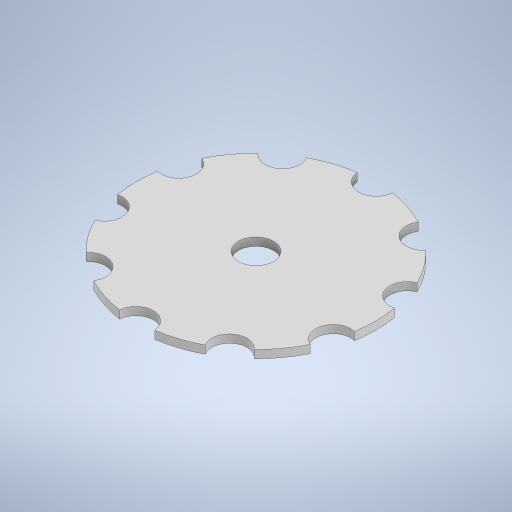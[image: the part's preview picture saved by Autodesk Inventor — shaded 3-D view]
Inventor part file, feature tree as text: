
AUTODESK INVENTOR PART (.ipt)
format: ipt  version: 2024.1 (Build 281209000, 209)  size: 281,600 bytes
history: native  units: mm
features: extrude x1, sketch x1
ambient origin geometry x8: Origin, YZ Plane, XZ Plane, XY Plane, X Axis, Y Axis, Z Axis, Center Point
bodies: Body1 (feature_tree)
feature tree (2):
  extrude  "押し出し2"  Depth=150.0mm
  sketch  "スケッチ1"
